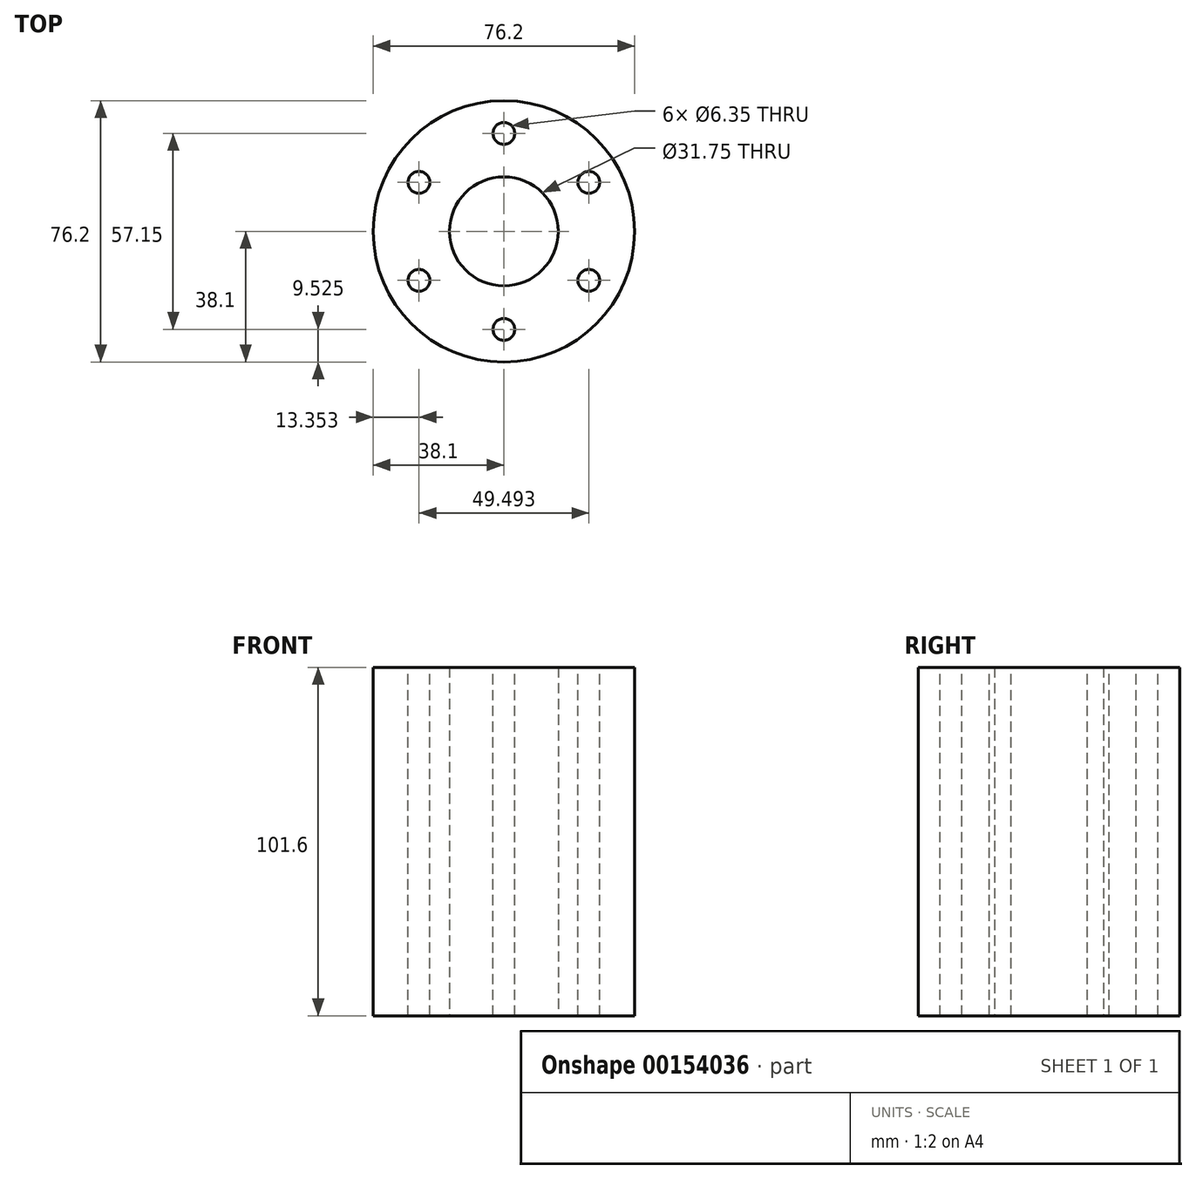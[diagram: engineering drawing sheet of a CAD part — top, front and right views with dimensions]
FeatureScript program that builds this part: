
annotation { "Feature Type Name" : "Feature", "Feature Type Description" : "" }
export const myFeature = defineFeature(function(context is Context, id is Id, definition is map)
    precondition{}
    {
        {
            var Q0;
            Q0=qCreatedBy(makeId("Top.planeOp"),FACE);
            var sketch = newSketch(context, id + "F0", { "sketchPlane" : qUnion([Q0])});
            skCircle(sketch, "E0", {"center": v(0, 0) * mm, "radius": 38.1 * mm});
            skCircle(sketch, "E1", {"center": v(0, 0) * mm, "radius": 15.88 * mm});
            skSolve(sketch);
        }
        {
            var Q0;
            Q0 = qSketchRegion(id + "F0", true);
            extrude(context, id + "F1", {"entities" : qUnion([Q0]), "depth" : 101.6 * mm});
        }
        {
            var Q0;
            Q0=makeQuery(id+"F1.opExtrude","CAP_FACE",FACE,{"disambiguationData":[OSD([sQuery(id+"F0.wireOp",EDGE,"E0"),sQuery(id+"F0.wireOp",EDGE,"E1")])],"isStart":false});
            var sketch = newSketch(context, id + "F2", { "sketchPlane" : qUnion([Q0])});
            skCircle(sketch, "E2", {"center": v(0, 28.58) * mm, "radius": 3.18 * mm});
            skCircle(sketch, "E3", {"center": v(0, 0) * mm, "radius": 28.58 * mm, "construction": true});
            skCircle(sketch, "E4.1.0", {"center": v(-24.75, 14.29) * mm, "radius": 3.18 * mm});
            skCircle(sketch, "E4.2.0", {"center": v(-24.75, -14.29) * mm, "radius": 3.18 * mm});
            skCircle(sketch, "E4.3.0", {"center": v(0, -28.58) * mm, "radius": 3.18 * mm});
            skCircle(sketch, "E4.4.0", {"center": v(24.75, -14.29) * mm, "radius": 3.18 * mm});
            skCircle(sketch, "E4.5.0", {"center": v(24.75, 14.29) * mm, "radius": 3.18 * mm});
            skSolve(sketch);
        }
        {
            var Q0;
            Q0 = qSketchRegion(id + "F2", true);
            extrude(context, id + "F3", {"entities" : qUnion([Q0]), "operationType" : NewBodyOperationType.REMOVE, "endBound" : BoundingType.THROUGH_ALL, "oppositeDirection" : true, "depth" : 76.83 * mm});
        }
    });
